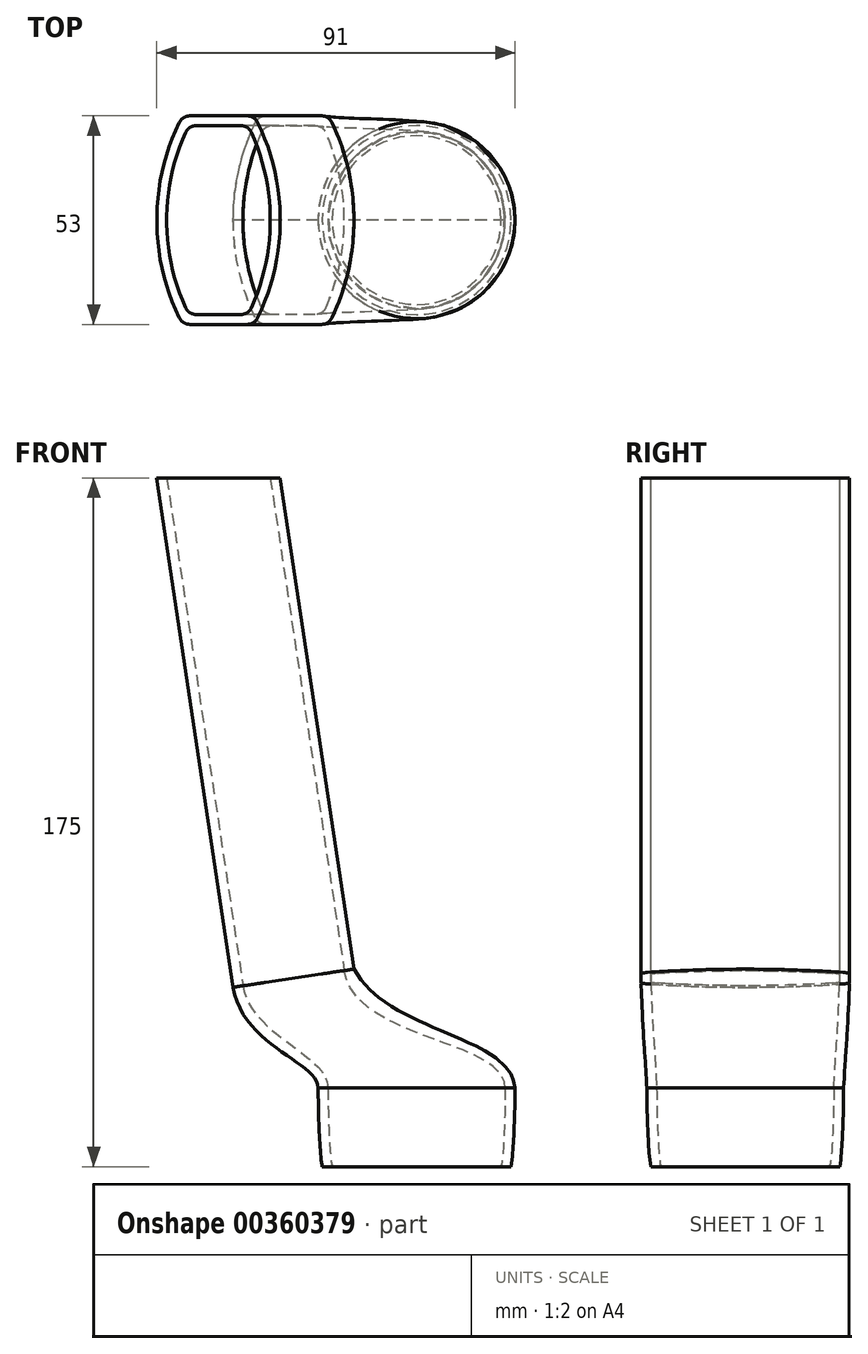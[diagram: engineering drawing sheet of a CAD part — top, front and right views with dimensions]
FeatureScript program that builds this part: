
annotation { "Feature Type Name" : "Feature", "Feature Type Description" : "" }
export const myFeature = defineFeature(function(context is Context, id is Id, definition is map)
    precondition{}
    {
        {
            var Q0;
            Q0=qCreatedBy(makeId("Top.planeOp"),FACE);
            var sketch = newSketch(context, id + "F0", { "sketchPlane" : qUnion([Q0])});
            skCircle(sketch, "E0", {"center": v(0, 0) * mm, "radius": 24 * mm});
            skSolve(sketch);
        }
        {
            var Q0;
            Q0=qCreatedBy(makeId("Top.planeOp"),FACE);
            cPlane(context, id + "F1", {"entities" : qUnion([Q0]), "cplaneType" : CPlaneType.OFFSET, "offset" : 20 * mm, "width" : 150 * mm, "height" : 150 * mm});
        }
        {
            var Q0;
            Q0=qCreatedBy(id+"F1.planeOp",FACE);
            var sketch = newSketch(context, id + "F2", { "sketchPlane" : qUnion([Q0])});
            skCircle(sketch, "E1", {"center": v(0, 0) * mm, "radius": 25 * mm});
            skSolve(sketch);
        }
        {
            var Q0;
            Q0=qCreatedBy(makeId("Front.planeOp"),FACE);
            var sketch = newSketch(context, id + "F3", { "sketchPlane" : qUnion([Q0])});
            skLineSegment(sketch, "E2.0", {"start": v(22.5, 20) * mm, "end": v(25, 20) * mm});
            skFitSpline(sketch, "E3", {"points": [v(24, 0) * mm, v(25, 20) * mm], "startDerivative": vector(2.1, 10.87) * mm, "endDerivative": vector(0, 15.67) * mm});
            skPoint(sketch, "E4", {"position": v(25, 3.62) * mm});
            skFitSpline(sketch, "E5.0", {"points": [v(21.55, 0.48) * mm, v(21.58, 0.65) * mm, v(21.65, 1.09) * mm, v(21.8, 2.23) * mm, v(21.97, 4.04) * mm, v(22.13, 6.64) * mm, v(22.27, 9.49) * mm, v(22.38, 12.42) * mm, v(22.47, 16.22) * mm, v(22.5, 18.72) * mm, v(22.5, 20) * mm]});
            skLineSegment(sketch, "E6", {"start": v(21.55, 0.48) * mm, "end": v(21.45, 0) * mm});
            skLineSegment(sketch, "E7", {"start": v(0, 0) * mm, "end": v(0, 12.52) * mm, "construction": true});
            skPoint(sketch, "E8.orphan", {"position": v(-25, 20) * mm});
            skLineSegment(sketch, "E9.trimOffspring", {"start": v(21.45, 0) * mm, "end": v(24, 0) * mm});
            skPoint(sketch, "E10.0.start.orphan", {"position": v(-24, 0) * mm});
            skSolve(sketch);
        }
        {
            var Q0;
            Q0=makeQuery(id+"F3.imprint","IMPRINT",FACE,{"disambiguationData":[TD([[makeQuery(id+"F3.imprint","IMPRINT",EDGE,{"derivedFrom":sQuery(id+"F3.wireOp",EDGE,"E2.0")}),-1.0]])]});
            var Q1;
            Q1=sQuery(id+"F3.wireOp",EDGE,"E7");
            revolve(context, id + "F4", {"entities" : qUnion([Q0]), "axis" : qUnion([Q1]), "revolveType" : RevolveType.FULL});
        }
        {
            var Q0;
            Q0=qCreatedBy(makeId("Front.planeOp"),FACE);
            var sketch = newSketch(context, id + "F5", { "sketchPlane" : qUnion([Q0])});
            skLineSegment(sketch, "E11.0", {"start": v(25, 20) * mm, "end": v(-25, 20) * mm});
            skLineSegment(sketch, "E12.0", {"start": v(24, 0) * mm, "end": v(-24, 0) * mm});
            skLineSegment(sketch, "E13", {"start": v(24, 0) * mm, "end": v(-46, 0) * mm});
            skLineSegment(sketch, "E14", {"start": v(24, 0) * mm, "end": v(-66, 0) * mm});
            skLineSegment(sketch, "E15", {"start": v(-66, 175) * mm, "end": v(-35.34, 179.6) * mm});
            skLineSegment(sketch, "E16", {"start": v(-50.67, 177.3) * mm, "end": v(-31.25, 47.9) * mm});
            skSolve(sketch);
        }
        {
            var Q0;
            Q0=sQuery(id+"F5.wireOp",EDGE,"E15");
            cPoint(context, id + "F6", {"entities" : qUnion([Q0]), "parameter" : 0.5});
        }
        {
            var Q0;
            Q0 = qCreatedBy(id + "F6" ,VERTEX);
            var Q1;
            Q1=sQuery(id+"F5.wireOp",EDGE,"E16");
            cPlane(context, id + "F7", {"entities" : qUnion([Q0, Q1]), "cplaneType" : CPlaneType.LINE_POINT, "offset" : 25 * mm, "width" : 150 * mm, "height" : 150 * mm});
        }
        {
            var Q0;
            Q0=qCreatedBy(id+"F7.planeOp",FACE);
            var sketch = newSketch(context, id + "F8", { "sketchPlane" : qUnion([Q0])});
            skPoint(sketch, "E17.0", {"position": v(-23.8, 0) * mm});
            skPoint(sketch, "E18.0", {"position": v(-8.3, 0) * mm});
            skPoint(sketch, "E19.0", {"position": v(-39.3, 0) * mm});
            skLineSegment(sketch, "E20", {"start": v(-23.8, 26.5) * mm, "end": v(-14.8, 26.5) * mm});
            skLineSegment(sketch, "E21", {"start": v(-23.8, 26.5) * mm, "end": v(-32.8, 26.5) * mm});
            skLineSegment(sketch, "E22", {"start": v(-23.8, -26.5) * mm, "end": v(-14.8, -26.5) * mm});
            skLineSegment(sketch, "E23", {"start": v(-23.8, -26.5) * mm, "end": v(-32.8, -26.5) * mm});
            skArc(sketch, "E24", {"start": v(-32.8, 26.5) * mm, "mid": v(-39.3, 0) * mm, "end": v(-32.8, -26.5) * mm});
            skArc(sketch, "E25.MirrorCS", {"start": v(-14.8, 26.5) * mm, "mid": v(-8.3, 0) * mm, "end": v(-14.8, -26.5) * mm});
            skLineSegment(sketch, "E26", {"start": v(-39.3, 0) * mm, "end": v(-36.8, 0) * mm});
            skLineSegment(sketch, "E27", {"start": v(-8.3, 0) * mm, "end": v(-10.8, 0) * mm});
            skLineSegment(sketch, "E28", {"start": v(-23.8, 0) * mm, "end": v(-23.8, -5.44) * mm, "construction": true});
            skSolve(sketch);
        }
        {
            var Q0;
            {var subQ3=sQuery(id+"F8.wireOp",EDGE,"E20");Q0=makeQuery(id+"F8.imprint","IMPRINT",FACE,{"disambiguationData":[TD([[makeQuery(id+"F8.imprint","IMPRINT",EDGE,{"derivedFrom":subQ3}),-1.0]])]});}
            var Q1;
            Q1=sQuery(id+"F5.wireOp",EDGE,"E16");
            sweep(context, id + "F9", {"profiles" : qUnion([Q0]), "path" : qUnion([Q1])});
        }
        {
            var Q0;
            Q0=qCreatedBy(makeId("Front.planeOp"),FACE);
            var sketch = newSketch(context, id + "F10", { "sketchPlane" : qUnion([Q0])});
            skLineSegment(sketch, "E29.0", {"start": v(-22.35, 49.23) * mm, "end": v(-15.92, 50.2) * mm});
            skLineSegment(sketch, "E30.0", {"start": v(-40.15, 46.56) * mm, "end": v(-46.58, 45.6) * mm});
            skLineSegment(sketch, "E31.0", {"start": v(25, 20) * mm, "end": v(-25, 20) * mm});
            skFitSpline(sketch, "E32", {"points": [v(-46.58, 45.6) * mm, v(-25, 20) * mm], "startDerivative": vector(6.72, -44.78) * mm, "endDerivative": vector(0, -19.98) * mm});
            skFitSpline(sketch, "E33", {"points": [v(-15.92, 50.2) * mm, v(25, 20) * mm], "startDerivative": vector(26.03, -48.66) * mm, "endDerivative": vector(2.66, -40.22) * mm});
            skSolve(sketch);
        }
        {
            var Q0;
            Q0=makeQuery(id+"F9.opSweep","CAP_FACE",FACE,{"disambiguationData":[OSD([sQuery(id+"F5.wireOp",VERTEX,"E16.start"),sQuery(id+"F8.wireOp",EDGE,"E20"),sQuery(id+"F8.wireOp",EDGE,"E21"),sQuery(id+"F8.wireOp",EDGE,"E22"),sQuery(id+"F8.wireOp",EDGE,"E23"),sQuery(id+"F8.wireOp",EDGE,"E24"),sQuery(id+"F8.wireOp",EDGE,"E25.MirrorCS")])],"isStart":true});
            var sketch = newSketch(context, id + "F11", { "sketchPlane" : qUnion([Q0])});
            skArc(sketch, "E34.0", {"start": v(-16.33, 24) * mm, "mid": v(-10.8, 0) * mm, "end": v(-16.33, -24) * mm});
            skArc(sketch, "E35.0", {"start": v(-31.26, -24) * mm, "mid": v(-36.8, 0) * mm, "end": v(-31.26, 24) * mm});
            skLineSegment(sketch, "E36.0", {"start": v(-31.26, 24) * mm, "end": v(-16.33, 24) * mm});
            skLineSegment(sketch, "E37.0", {"start": v(-16.33, -24) * mm, "end": v(-31.26, -24) * mm});
            skSolve(sketch);
        }
        {
            var Q0;
            Q0 = qSketchRegion(id + "F11", true);
            var Q1;
            Q1=sQuery(id+"F5.wireOp",EDGE,"E16");
            sweep(context, id + "F12", {"operationType" : NewBodyOperationType.REMOVE, "profiles" : qUnion([Q0]), "path" : qUnion([Q1])});
        }
        {
            var Q0;
            Q0=qCreatedBy(makeId("Front.planeOp"),FACE);
            var sketch = newSketch(context, id + "F13", { "sketchPlane" : qUnion([Q0])});
            skLineSegment(sketch, "E38.0", {"start": v(-23.87, 49) * mm, "end": v(-18.4, 49.82) * mm});
            skLineSegment(sketch, "E39.0", {"start": v(-38.63, 46.78) * mm, "end": v(-44.1, 45.96) * mm});
            skLineSegment(sketch, "E40.0", {"start": v(22.5, 20) * mm, "end": v(-22.5, 20) * mm});
            skFitSpline(sketch, "E41", {"points": [v(-18.4, 49.82) * mm, v(22.5, 20) * mm], "startDerivative": vector(7.95, -52.96) * mm, "endDerivative": vector(0, -37.08) * mm});
            skFitSpline(sketch, "E42", {"points": [v(-44.1, 45.96) * mm, v(-22.5, 20) * mm], "startDerivative": vector(5.7, -37.96) * mm, "endDerivative": vector(0, -25.64) * mm});
            skSolve(sketch);
        }
        {
            var Q0;
            Q0=makeQuery(id+"F9.opSweep","SWEPT_EDGE",EDGE,{"disambiguationData":[OSD([sQuery(id+"F5.wireOp",EDGE,"E16"),sQuery(id+"F8.wireOp",EDGE,"E20"),sQuery(id+"F8.wireOp",EDGE,"E25.MirrorCS")])]});
            var Q1;
            Q1=makeQuery(id+"F9.opSweep","SWEPT_EDGE",EDGE,{"disambiguationData":[OSD([sQuery(id+"F5.wireOp",EDGE,"E16"),sQuery(id+"F8.wireOp",EDGE,"E21"),sQuery(id+"F8.wireOp",EDGE,"E24")])]});
            var Q2;
            Q2=makeQuery(id+"F9.opSweep","SWEPT_EDGE",EDGE,{"disambiguationData":[OSD([sQuery(id+"F5.wireOp",EDGE,"E16"),sQuery(id+"F8.wireOp",EDGE,"E22"),sQuery(id+"F8.wireOp",EDGE,"E25.MirrorCS")])]});
            var Q3;
            Q3=makeQuery(id+"F9.opSweep","SWEPT_EDGE",EDGE,{"disambiguationData":[OSD([sQuery(id+"F5.wireOp",EDGE,"E16"),sQuery(id+"F8.wireOp",EDGE,"E23"),sQuery(id+"F8.wireOp",EDGE,"E24")])]});
            var Q4;
            Q4=makeQuery(id+"F12.boolean.opBoolean","COPY",EDGE,{"derivedFrom":makeQuery(id+"F12.opSweep","SWEPT_EDGE",EDGE,{"disambiguationData":[OSD([sQuery(id+"F5.wireOp",EDGE,"E16"),sQuery(id+"F11.wireOp",EDGE,"E34.0"),sQuery(id+"F11.wireOp",EDGE,"E37.0")])]})});
            var Q5;
            Q5=makeQuery(id+"F12.boolean.opBoolean","COPY",EDGE,{"derivedFrom":makeQuery(id+"F12.opSweep","SWEPT_EDGE",EDGE,{"disambiguationData":[OSD([sQuery(id+"F5.wireOp",EDGE,"E16"),sQuery(id+"F11.wireOp",EDGE,"E34.0"),sQuery(id+"F11.wireOp",EDGE,"E36.0")])]})});
            var Q6;
            Q6=makeQuery(id+"F12.boolean.opBoolean","COPY",EDGE,{"derivedFrom":makeQuery(id+"F12.opSweep","SWEPT_EDGE",EDGE,{"disambiguationData":[OSD([sQuery(id+"F5.wireOp",EDGE,"E16"),sQuery(id+"F11.wireOp",EDGE,"E35.0"),sQuery(id+"F11.wireOp",EDGE,"E36.0")])]})});
            var Q7;
            Q7=makeQuery(id+"F12.boolean.opBoolean","COPY",EDGE,{"derivedFrom":makeQuery(id+"F12.opSweep","SWEPT_EDGE",EDGE,{"disambiguationData":[OSD([sQuery(id+"F5.wireOp",EDGE,"E16"),sQuery(id+"F11.wireOp",EDGE,"E35.0"),sQuery(id+"F11.wireOp",EDGE,"E37.0")])]})});
            fillet(context, id + "F14", {"entities" : qUnion([Q0, Q1, Q2, Q3, Q4, Q5, Q6, Q7]), "radius" : 3 * mm, "tangentPropagation" : true, "allowEdgeOverflow" : false});
        }
        {
            var Q0;
            Q0=makeQuery(id+"F9.opSweep","CAP_FACE",FACE,{"disambiguationData":[OSD([sQuery(id+"F5.wireOp",VERTEX,"E16.end"),sQuery(id+"F8.wireOp",EDGE,"E20"),sQuery(id+"F8.wireOp",EDGE,"E21"),sQuery(id+"F8.wireOp",EDGE,"E22"),sQuery(id+"F8.wireOp",EDGE,"E23"),sQuery(id+"F8.wireOp",EDGE,"E24"),sQuery(id+"F8.wireOp",EDGE,"E25.MirrorCS")])],"isStart":false});
            var sketch = newSketch(context, id + "F15", { "sketchPlane" : qUnion([Q0])});
            skLineSegment(sketch, "E43.0", {"start": v(-16.65, 26.5) * mm, "end": v(-30.94, 26.5) * mm});
            skArc(sketch, "E44.0", {"start": v(-13.94, -24.8) * mm, "mid": v(-8.3, 0) * mm, "end": v(-13.94, 24.8) * mm});
            skArc(sketch, "E45.0", {"start": v(-33.65, 24.8) * mm, "mid": v(-39.3, 0) * mm, "end": v(-33.65, -24.8) * mm});
            skLineSegment(sketch, "E46.0", {"start": v(-30.94, -26.5) * mm, "end": v(-16.65, -26.5) * mm});
            skArc(sketch, "E47.0", {"start": v(-13.94, 24.8) * mm, "mid": v(-15.05, 26.04) * mm, "end": v(-16.65, 26.5) * mm});
            skPoint(sketch, "E48.0", {"position": v(-32.54, 26.04) * mm});
            skArc(sketch, "E49.0", {"start": v(-30.94, 26.5) * mm, "mid": v(-32.54, 26.04) * mm, "end": v(-33.65, 24.8) * mm});
            skPoint(sketch, "E50.orphan", {"position": v(-32.8, 26.5) * mm});
            skArc(sketch, "E51.0", {"start": v(-16.65, -26.5) * mm, "mid": v(-15.05, -26.04) * mm, "end": v(-13.94, -24.8) * mm});
            skArc(sketch, "E52.0", {"start": v(-33.65, -24.8) * mm, "mid": v(-32.54, -26.04) * mm, "end": v(-30.94, -26.5) * mm});
            skSolve(sketch);
        }
        {
            var Q0;
            Q0=makeQuery(id+"F15.imprint","IMPRINT",FACE,{"disambiguationData":[TD([[makeQuery(id+"F15.imprint","IMPRINT",EDGE,{"derivedFrom":sQuery(id+"F15.wireOp",EDGE,"E43.0")}),1.0]])]});
            var sketch = newSketch(context, id + "F16", { "sketchPlane" : qUnion([Q0])});
            skArc(sketch, "E53.0", {"start": v(-15.5, -22.22) * mm, "mid": v(-10.8, 0) * mm, "end": v(-15.5, 22.22) * mm});
            skLineSegment(sketch, "E54.0", {"start": v(-18.24, 24) * mm, "end": v(-29.34, 24) * mm});
            skArc(sketch, "E55.0", {"start": v(-32.09, 22.22) * mm, "mid": v(-36.8, 0) * mm, "end": v(-32.09, -22.22) * mm});
            skLineSegment(sketch, "E56.0", {"start": v(-29.34, -24) * mm, "end": v(-18.24, -24) * mm});
            skArc(sketch, "E57.0", {"start": v(-15.5, -22.22) * mm, "mid": v(-16.6, -23.52) * mm, "end": v(-18.24, -24) * mm});
            skArc(sketch, "E58.0", {"start": v(-29.34, -24) * mm, "mid": v(-30.98, -23.52) * mm, "end": v(-32.09, -22.22) * mm});
            skPoint(sketch, "E59.0", {"position": v(-16.6, 23.52) * mm});
            skArc(sketch, "E60.0", {"start": v(-32.09, 22.22) * mm, "mid": v(-30.98, 23.52) * mm, "end": v(-29.34, 24) * mm});
            skArc(sketch, "E61.0", {"start": v(-18.24, 24) * mm, "mid": v(-16.6, 23.52) * mm, "end": v(-15.5, 22.22) * mm});
            skPoint(sketch, "E62.orphan", {"position": v(-16.33, 24) * mm});
            skPoint(sketch, "E63.orphan", {"position": v(-31.26, 24) * mm});
            skSolve(sketch);
        }
        {
            var Q0;
            Q0=makeQuery(id+"F4.opRevolve","SWEPT_FACE",FACE,{"disambiguationData":[OSD([sQuery(id+"F3.wireOp",EDGE,"E2.0")])]});
            var sketch = newSketch(context, id + "F17", { "sketchPlane" : qUnion([Q0])});
            skCircle(sketch, "E64.0", {"center": v(0, 0) * mm, "radius": 22.5 * mm});
            skSolve(sketch);
        }
        {
            var Q0;
            Q0 = qSketchRegion(id + "F2", true);
            var Q1;
            Q1 = qSketchRegion(id + "F15", true);
            var Q2;
            Q2=sQuery(id+"F10.wireOp",EDGE,"E32");
            var Q3;
            Q3=sQuery(id+"F10.wireOp",EDGE,"E33");
            loft(context, id + "F18", {"addGuides" : true, "sheetProfilesArray" : [{ "sheetProfileEntities" : qUnion([Q0]) }, { "sheetProfileEntities" : qUnion([Q1]) }], "guidesArray" : [{ "guideEntities" : qUnion([Q2]), "guideDerivativeType" : LoftGuideDerivativeType.DEFAULT, "guideDerivativeMagnitude" : 1 }, { "guideEntities" : qUnion([Q3]), "guideDerivativeType" : LoftGuideDerivativeType.DEFAULT, "guideDerivativeMagnitude" : 1 }]});
        }
        {
            var Q0;
            Q0 = qSketchRegion(id + "F17", true);
            var Q1;
            Q1 = qSketchRegion(id + "F16", true);
            var Q2;
            Q2=sQuery(id+"F13.wireOp",EDGE,"E41");
            var Q3;
            Q3=sQuery(id+"F13.wireOp",EDGE,"E42");
            loft(context, id + "F19", {"operationType" : NewBodyOperationType.REMOVE, "addGuides" : true, "sheetProfilesArray" : [{ "sheetProfileEntities" : qUnion([Q0]) }, { "sheetProfileEntities" : qUnion([Q1]) }], "guidesArray" : [{ "guideEntities" : qUnion([Q2]), "guideDerivativeType" : LoftGuideDerivativeType.DEFAULT, "guideDerivativeMagnitude" : 1 }, { "guideEntities" : qUnion([Q3]), "guideDerivativeType" : LoftGuideDerivativeType.DEFAULT, "guideDerivativeMagnitude" : 1 }]});
        }
        {
            var Q0;
            Q0=makeQuery(id+"F9.opSweep","SWEPT_FACE",FACE,{"disambiguationData":[OSD([sQuery(id+"F5.wireOp",EDGE,"E16"),sQuery(id+"F8.wireOp",EDGE,"E20"),sQuery(id+"F8.wireOp",EDGE,"E21")])]});
            var sketch = newSketch(context, id + "F20", { "sketchPlane" : qUnion([Q0])});
            skLineSegment(sketch, "E65.0", {"start": v(-43.6, 178.36) * mm, "end": v(-57.74, 176.24) * mm});
            skLineSegment(sketch, "E66.0", {"start": v(-60.41, 175.84) * mm, "end": v(-66, 175) * mm});
            skLineSegment(sketch, "E67.0", {"start": v(-60.41, 175.84) * mm, "end": v(-57.74, 176.24) * mm});
            skLineSegment(sketch, "E68.0", {"start": v(-43.6, 178.36) * mm, "end": v(-40.93, 178.76) * mm});
            skLineSegment(sketch, "E69.0", {"start": v(-40.93, 178.76) * mm, "end": v(-35.34, 179.6) * mm});
            skLineSegment(sketch, "E70", {"start": v(-66, 175) * mm, "end": v(-30.96, 175) * mm});
            skLineSegment(sketch, "E71", {"start": v(-30.96, 175) * mm, "end": v(-30.96, 180.26) * mm});
            skLineSegment(sketch, "E72", {"start": v(-35.34, 179.6) * mm, "end": v(-30.96, 180.26) * mm});
            skSolve(sketch);
        }
        {
            var Q0;
            Q0 = qSketchRegion(id + "F20", true);
            extrude(context, id + "F21", {"entities" : qUnion([Q0]), "operationType" : NewBodyOperationType.REMOVE, "oppositeDirection" : true, "depth" : 60.4 * mm});
        }
    });
